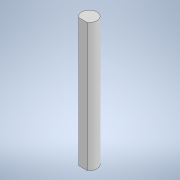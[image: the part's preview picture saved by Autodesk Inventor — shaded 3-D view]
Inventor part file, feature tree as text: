
AUTODESK INVENTOR PART (.ipt)
format: ipt  version: 2020 (Build 240168000, 168)  size: 96,768 bytes
history: native  units: in
note: dims shown in document units (in); Inventor stores cm internally (conversion verified against a paired STEP export)
features: extrude x2, sketch x2
ambient origin geometry x8: Origin, YZ Plane, XZ Plane, XY Plane, X Axis, Y Axis, Z Axis, Center Point
bodies: Solid1 (feature_tree)
feature tree (4):
  extrude  "Extrusion1"  Depth=1.5748in TaperAngle=0.0deg
  extrude  "Extrusion2"  [1 undecoded]
  sketch  "Sketch1"  dims[d0=0.187in d1=1.5748in d2=0.0in]
  sketch  "Sketch2"  dims[d3=1.5748in d4=0.0in]
note: 1 required parameter value undecoded (feature->parameter linkage not recoverable at this tier; creation-order binding heuristic only, values carry confidence <= 0.55)
